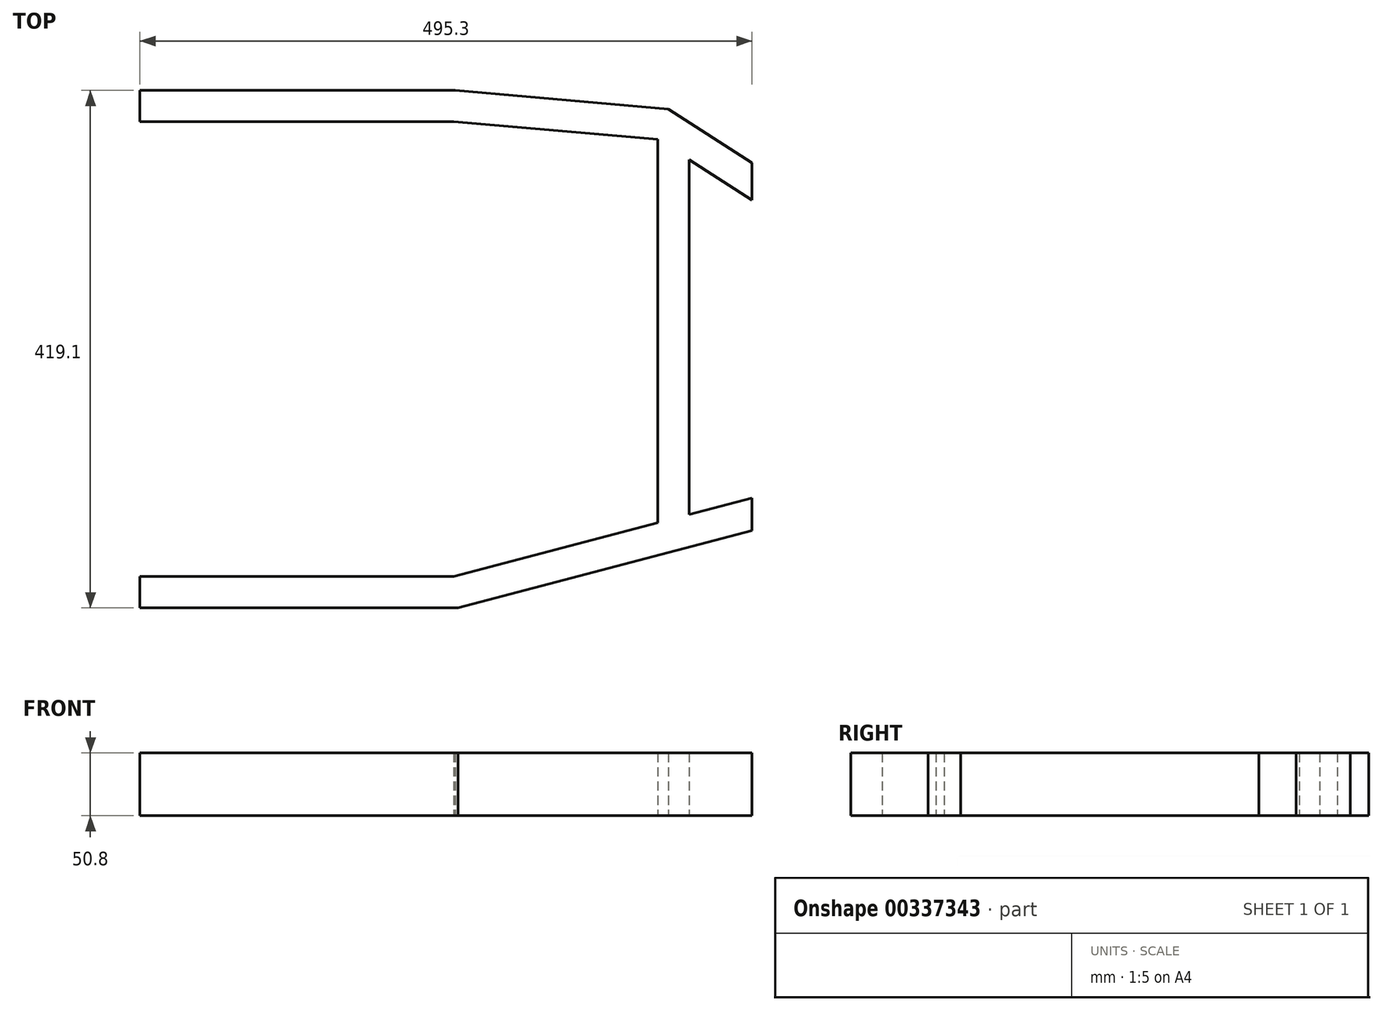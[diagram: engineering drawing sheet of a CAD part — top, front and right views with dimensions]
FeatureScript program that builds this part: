
annotation { "Feature Type Name" : "Feature", "Feature Type Description" : "" }
export const myFeature = defineFeature(function(context is Context, id is Id, definition is map)
    precondition{}
    {
        {
            var Q0;
            Q0=qCreatedBy(makeId("Top.planeOp"),FACE);
            var sketch = newSketch(context, id + "F0", { "sketchPlane" : qUnion([Q0])});
            skLineSegment(sketch, "E0", {"start": v(-183.97, 182.12) * mm, "end": v(70.03, 182.12) * mm});
            skLineSegment(sketch, "E1", {"start": v(311.33, -122.68) * mm, "end": v(70.03, -186.18) * mm});
            skLineSegment(sketch, "E2", {"start": v(70.03, -186.18) * mm, "end": v(-183.97, -186.18) * mm});
            skLineSegment(sketch, "E3", {"start": v(-183.97, -186.18) * mm, "end": v(-183.97, 182.12) * mm, "construction": true});
            skLineSegment(sketch, "E4", {"start": v(-183.97, -2.03) * mm, "end": v(311.33, -2.03) * mm, "construction": true});
            skLineSegment(sketch, "E5.bottom", {"start": v(565.9, 185.54) * mm, "end": v(591.3, 185.54) * mm});
            skLineSegment(sketch, "E5.top", {"start": v(565.9, 134.74) * mm, "end": v(591.3, 134.74) * mm});
            skLineSegment(sketch, "E5.left", {"start": v(565.9, 185.54) * mm, "end": v(565.9, 134.74) * mm});
            skLineSegment(sketch, "E5.right", {"start": v(591.3, 185.54) * mm, "end": v(591.3, 134.74) * mm});
            skLineSegment(sketch, "E6", {"start": v(591.3, 185.54) * mm, "end": v(686, 185.54) * mm});
            skCircle(sketch, "E7", {"center": v(629.4, 223.64) * mm, "radius": 38.1 * mm});
            skLineSegment(sketch, "E8", {"start": v(591.3, 185.54) * mm, "end": v(591.3, 268.8) * mm});
            skLineSegment(sketch, "E9", {"start": v(591.3, 134.74) * mm, "end": v(629.4, 134.74) * mm});
            skLineSegment(sketch, "E10", {"start": v(629.4, 185.54) * mm, "end": v(629.4, 134.74) * mm});
            skPoint(sketch, "E10.endSnap0", {"position": v(638.65, 134.74) * mm});
            skPoint(sketch, "E11.orphan", {"position": v(686, 134.74) * mm});
            skLineSegment(sketch, "E12.bottom", {"start": v(-285.57, 156.72) * mm, "end": v(-82.37, 156.72) * mm});
            skLineSegment(sketch, "E12.top", {"start": v(-285.57, 149.86) * mm, "end": v(-82.37, 149.86) * mm});
            skLineSegment(sketch, "E12.left", {"start": v(-285.57, 156.72) * mm, "end": v(-285.57, 149.86) * mm});
            skLineSegment(sketch, "E12.right", {"start": v(-82.37, 156.72) * mm, "end": v(-82.37, 149.86) * mm});
            skLineSegment(sketch, "E13.bottom", {"start": v(-285.57, 161.42) * mm, "end": v(-82.37, 161.42) * mm});
            skLineSegment(sketch, "E13.top", {"start": v(-285.57, 145.16) * mm, "end": v(-82.37, 145.16) * mm});
            skLineSegment(sketch, "E13.left", {"start": v(-285.57, 161.42) * mm, "end": v(-285.57, 145.16) * mm});
            skLineSegment(sketch, "E13.right", {"start": v(-82.37, 161.42) * mm, "end": v(-82.37, 145.16) * mm});
            skLineSegment(sketch, "E14", {"start": v(-285.57, 153.3) * mm, "end": v(-82.37, 153.3) * mm, "construction": true});
            skLineSegment(sketch, "E15", {"start": v(-183.97, 156.72) * mm, "end": v(-183.97, 182.12) * mm, "construction": true});
            skPoint(sketch, "E15.endSnap0", {"position": v(-183.97, 161.42) * mm});
            skLineSegment(sketch, "E16", {"start": v(-183.97, 101.6) * mm, "end": v(235.13, 101.6) * mm});
            skLineSegment(sketch, "E17", {"start": v(70.03, 182.12) * mm, "end": v(235.13, 167.77) * mm});
            skLineSegment(sketch, "E18", {"start": v(235.13, 167.77) * mm, "end": v(311.33, 118.62) * mm});
            skLineSegment(sketch, "E19.bottom", {"start": v(158.93, 161.42) * mm, "end": v(235.13, 161.42) * mm});
            skLineSegment(sketch, "E19.top", {"start": v(158.93, 145.16) * mm, "end": v(235.13, 145.16) * mm});
            skLineSegment(sketch, "E19.left", {"start": v(158.93, 161.42) * mm, "end": v(158.93, 145.16) * mm});
            skLineSegment(sketch, "E19.right", {"start": v(235.13, 161.42) * mm, "end": v(235.13, 145.16) * mm});
            skLineSegment(sketch, "E20.0", {"start": v(243.6, 192.53) * mm, "end": v(311.33, 148.84) * mm});
            skLineSegment(sketch, "E20.1", {"start": v(71.13, 207.52) * mm, "end": v(243.6, 192.53) * mm});
            skLineSegment(sketch, "E20.2", {"start": v(-183.97, 207.52) * mm, "end": v(71.13, 207.52) * mm});
            skLineSegment(sketch, "E21.0", {"start": v(73.32, -211.58) * mm, "end": v(-183.97, -211.58) * mm});
            skLineSegment(sketch, "E21.1", {"start": v(311.33, -148.95) * mm, "end": v(73.32, -211.58) * mm});
            skLineSegment(sketch, "E22", {"start": v(-183.97, 207.52) * mm, "end": v(-183.97, 182.12) * mm});
            skLineSegment(sketch, "E23", {"start": v(-183.97, -186.18) * mm, "end": v(-183.97, -211.58) * mm});
            skLineSegment(sketch, "E24", {"start": v(235.13, 167.77) * mm, "end": v(243.6, 192.53) * mm});
            skLineSegment(sketch, "E25", {"start": v(311.33, 148.84) * mm, "end": v(311.33, 118.62) * mm});
            skLineSegment(sketch, "E26", {"start": v(311.33, -122.68) * mm, "end": v(311.33, -148.95) * mm});
            skLineSegment(sketch, "E27", {"start": v(70.03, -186.18) * mm, "end": v(73.32, -211.58) * mm});
            skLineSegment(sketch, "E28.left", {"start": v(235.13, 167.77) * mm, "end": v(235.13, -142.73) * mm});
            skLineSegment(sketch, "E28.right", {"start": v(260.53, 151.39) * mm, "end": v(260.53, -136.05) * mm});
            skLineSegment(sketch, "E29", {"start": v(158.93, 145.16) * mm, "end": v(-183.97, 145.16) * mm, "construction": true});
            skLineSegment(sketch, "E30", {"start": v(71.13, 207.52) * mm, "end": v(70.03, 182.12) * mm});
            skLineSegment(sketch, "E31", {"start": v(235.13, -2.03) * mm, "end": v(235.13, -142.73) * mm});
            skLineSegment(sketch, "E32", {"start": v(235.13, 167.77) * mm, "end": v(235.13, -2.03) * mm});
            skSolve(sketch);
        }
        {
            var Q0;
            Q0=makeQuery(id+"F0.imprint","IMPRINT",FACE,{"disambiguationData":[TD([[makeQuery(id+"F0.imprint","IMPRINT",EDGE,{"derivedFrom":sQuery(id+"F0.wireOp",EDGE,"E0")}),1.0]])]});
            var Q1;
            Q1=makeQuery(id+"F0.imprint","IMPRINT",FACE,{"disambiguationData":[TD([[makeQuery(id+"F0.imprint","IMPRINT",EDGE,{"derivedFrom":sQuery(id+"F0.wireOp",EDGE,"E17")}),1.0]])]});
            var Q2;
            Q2=makeQuery(id+"F0.imprint","IMPRINT",FACE,{"disambiguationData":[TD([[makeQuery(id+"F0.imprint","IMPRINT",EDGE,{"derivedFrom":sQuery(id+"F0.wireOp",EDGE,"E20.0")}),-1.0]])]});
            var Q3;
            {var subQ4=sQuery(id+"F0.wireOp",EDGE,"E28.right");Q3=makeQuery(id+"F0.imprint","IMPRINT",FACE,{"disambiguationData":[TD([[makeQuery(id+"F0.imprint","IMPRINT",EDGE,{"derivedFrom":subQ4}),-1.0]])]});}
            var Q4;
            Q4=makeQuery(id+"F0.imprint","IMPRINT",FACE,{"disambiguationData":[TD([[makeQuery(id+"F0.imprint","IMPRINT",EDGE,{"derivedFrom":sQuery(id+"F0.wireOp",EDGE,"E21.1")}),-1.0]])]});
            var Q5;
            Q5=makeQuery(id+"F0.imprint","IMPRINT",FACE,{"disambiguationData":[TD([[makeQuery(id+"F0.imprint","IMPRINT",EDGE,{"derivedFrom":sQuery(id+"F0.wireOp",EDGE,"E2")}),1.0]])]});
            extrude(context, id + "F1", {"entities" : qUnion([Q0, Q1, Q2, Q3, Q4, Q5]), "endBound" : BoundingType.SYMMETRIC, "depth" : 50.8 * mm});
        }
    });
